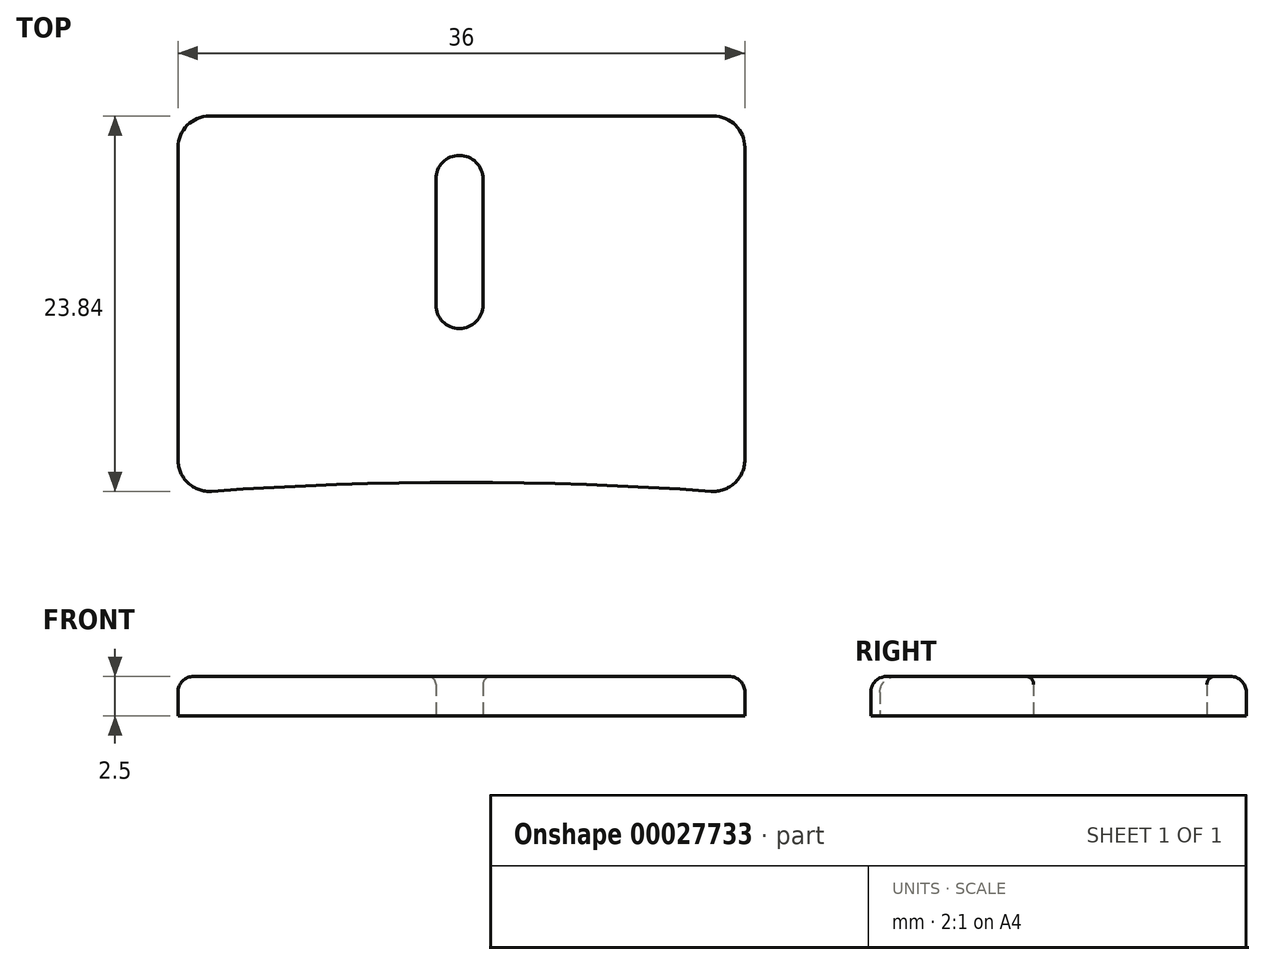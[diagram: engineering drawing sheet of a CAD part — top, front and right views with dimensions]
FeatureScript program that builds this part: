
annotation { "Feature Type Name" : "Feature", "Feature Type Description" : "" }
export const myFeature = defineFeature(function(context is Context, id is Id, definition is map)
    precondition{}
    {
        {
            var Q0;
            Q0=qCreatedBy(makeId("Top.planeOp"),FACE);
            var sketch = newSketch(context, id + "F0", { "sketchPlane" : qUnion([Q0])});
            skLineSegment(sketch, "E0.bottom", {"start": v(6.3, 18.2) * mm, "end": v(38.3, 18.2) * mm});
            skLineSegment(sketch, "E0.left", {"start": v(4.3, 16.2) * mm, "end": v(4.3, -3.65) * mm});
            skLineSegment(sketch, "E0.right", {"start": v(40.3, 16.2) * mm, "end": v(40.3, -3.65) * mm});
            skArc(sketch, "E1", {"start": v(38.16, -5.64) * mm, "mid": v(22.3, -5.07) * mm, "end": v(6.45, -5.64) * mm});
            skLineSegment(sketch, "E2.bottom", {"start": v(22.18, 15.7) * mm, "end": v(22.18, 15.7) * mm});
            skLineSegment(sketch, "E2.top", {"start": v(22.18, 4.7) * mm, "end": v(22.18, 4.7) * mm});
            skLineSegment(sketch, "E2.left", {"start": v(20.68, 14.2) * mm, "end": v(20.68, 6.2) * mm});
            skLineSegment(sketch, "E2.right", {"start": v(23.68, 14.2) * mm, "end": v(23.68, 6.2) * mm});
            skPoint(sketch, "E3.visualSharp", {"position": v(4.3, 18.2) * mm});
            skArc(sketch, "E3.filletArc", {"start": v(6.3, 18.2) * mm, "mid": v(4.9, 17.6) * mm, "end": v(4.3, 16.2) * mm});
            skPoint(sketch, "E4.visualSharp", {"position": v(4.3, -5.8) * mm});
            skArc(sketch, "E4.filletArc", {"start": v(4.3, -3.65) * mm, "mid": v(4.95, -5.11) * mm, "end": v(6.45, -5.64) * mm});
            skPoint(sketch, "E5.visualSharp", {"position": v(40.3, -5.8) * mm});
            skArc(sketch, "E5.filletArc", {"start": v(38.16, -5.64) * mm, "mid": v(39.67, -5.11) * mm, "end": v(40.3, -3.65) * mm});
            skPoint(sketch, "E6.visualSharp", {"position": v(40.3, 18.2) * mm});
            skArc(sketch, "E6.filletArc", {"start": v(40.3, 16.2) * mm, "mid": v(39.72, 17.6) * mm, "end": v(38.3, 18.2) * mm});
            skPoint(sketch, "E7.visualSharp", {"position": v(20.68, 4.7) * mm});
            skArc(sketch, "E7.filletArc", {"start": v(20.68, 6.2) * mm, "mid": v(21.12, 5.13) * mm, "end": v(22.18, 4.7) * mm});
            skPoint(sketch, "E8.visualSharp", {"position": v(23.68, 4.7) * mm});
            skArc(sketch, "E8.filletArc", {"start": v(22.18, 4.7) * mm, "mid": v(23.24, 5.13) * mm, "end": v(23.68, 6.2) * mm});
            skPoint(sketch, "E9.visualSharp", {"position": v(23.68, 15.7) * mm});
            skArc(sketch, "E9.filletArc", {"start": v(23.68, 14.2) * mm, "mid": v(23.24, 15.25) * mm, "end": v(22.18, 15.7) * mm});
            skPoint(sketch, "E10.visualSharp", {"position": v(20.68, 15.7) * mm});
            skArc(sketch, "E10.filletArc", {"start": v(22.18, 15.7) * mm, "mid": v(21.12, 15.25) * mm, "end": v(20.68, 14.2) * mm});
            skSolve(sketch);
        }
        {
            var Q0;
            Q0=makeQuery(id+"F0.imprint","IMPRINT",FACE,{"disambiguationData":[TD([[makeQuery(id+"F0.imprint","IMPRINT",EDGE,{"derivedFrom":sQuery(id+"F0.wireOp",EDGE,"E0.bottom")}),-1.0]])]});
            extrude(context, id + "F1", {"entities" : qUnion([Q0]), "depth" : 2.5 * mm});
        }
        {
            var Q0;
            Q0=makeQuery(id+"F1.opExtrude","CAP_EDGE",EDGE,{"disambiguationData":[OSD([sQuery(id+"F0.wireOp",EDGE,"E1")])],"isStart":false});
            fillet(context, id + "F2", {"entities" : qUnion([Q0]), "radius" : 1 * mm, "tangentPropagation" : true, "allowEdgeOverflow" : false});
        }
        {
            var Q0;
            Q0=makeQuery(id+"F1.opExtrude","CAP_EDGE",EDGE,{"disambiguationData":[OSD([sQuery(id+"F0.wireOp",EDGE,"E2.left")])],"isStart":false});
            fillet(context, id + "F3", {"entities" : qUnion([Q0]), "radius" : .5 * mm, "tangentPropagation" : true, "allowEdgeOverflow" : false});
        }
    });
